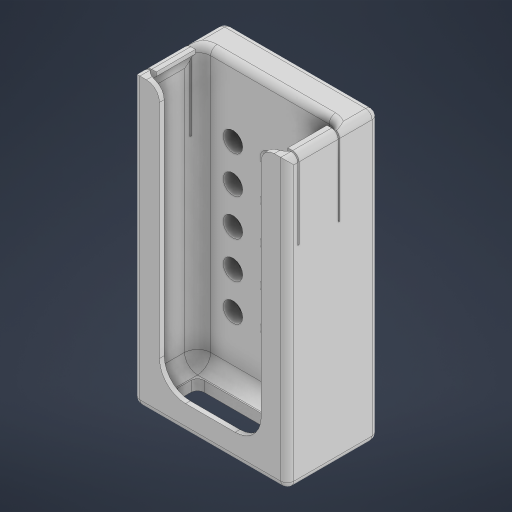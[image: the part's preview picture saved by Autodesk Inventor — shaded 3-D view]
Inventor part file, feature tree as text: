
AUTODESK INVENTOR PART (.ipt)
format: ipt  version: 2023 (Build 270158000, 158)  size: 419,328 bytes
history: native  units: in
note: dims shown in document units (in); Inventor stores cm internally (conversion verified against a paired STEP export)
features: sketch x7, extrude x6, fillet x4, projected_geometry x2, mirror x1, hole x1, pattern_linear x1
ambient origin geometry x8: Origin, YZ Plane, XZ Plane, XY Plane, X Axis, Y Axis, Z Axis, Center Point
bodies: Solid1 (feature_tree)
feature tree (22):
  extrude  "Extrusion1"  Depth=5.3in
  extrude  "Extrusion2"  Depth=1.75in TaperAngle=0.0deg
  extrude  "Extrusion3"  Depth=0.09in
  fillet  "Fillet1"  Radius=0.09in
  extrude  "Extrusion4"  Depth=5.3in TaperAngle=0.0deg
  extrude  "Extrusion5"  Depth=0.5in
  mirror  "Mirror1"
  extrude  "Extrusion6"  Depth=0.5in TaperAngle=0.0deg
  hole  "Hole1"  [1 undecoded]
  pattern_linear  "Rectangular Pattern1"  Spacing1=0.025in  [1 undecoded]
  fillet  "Fillet2"  Radius=0.025in
  fillet  "Fillet3"  Radius=0.75in
  fillet  "Fillet4"  Radius=1.5in
  sketch  "Sketch1"  dims[d0=2.75in d1=5.3in]
  sketch  "Sketch2"  dims[d2=0.1in d3=1.75in d4=0.0in]
  sketch  "Sketch3"  dims[d5=0.09in d6=0.09in d7=0.09in]
  sketch  "Sketch4"  dims[d8=1.05in d9=5.3in d10=0.0in]
  sketch  "Sketch5"  dims[d11=0.5in d12=0.5in]
  projected_geometry  "Projected Loop1"
  sketch  "Sketch6"  dims[d13=0.5in d14=5.25in d15=0.0in]
  projected_geometry  "Projected Loop2"
  sketch  "Sketch7"  dims[d16=0.25in d17=0.2in d18=0.025in d19=0.025in d20=0.75in d21=1.5in d22=0.0in d23=0.0in d30=1.0in d31=0.0in d32=0.125in d33=0.05in d35=0.375in d36=0.375in d37=0.025in d38=0.025in d39=1.0in d40=0.0in d42=0.707in d43=1.414in d44=0.156in d45=0.38in d46=0.375in d47=0.25in d48=0.5635in d49=1.0in d50=0.8108in d51=1.1811in d53=0.707in d54=1.9685in d56=0.707in d57=0.5in d58=0.25in d59=0.125in]
note: 2 required parameter values undecoded (feature->parameter linkage not recoverable at this tier; creation-order binding heuristic only, values carry confidence <= 0.55)
